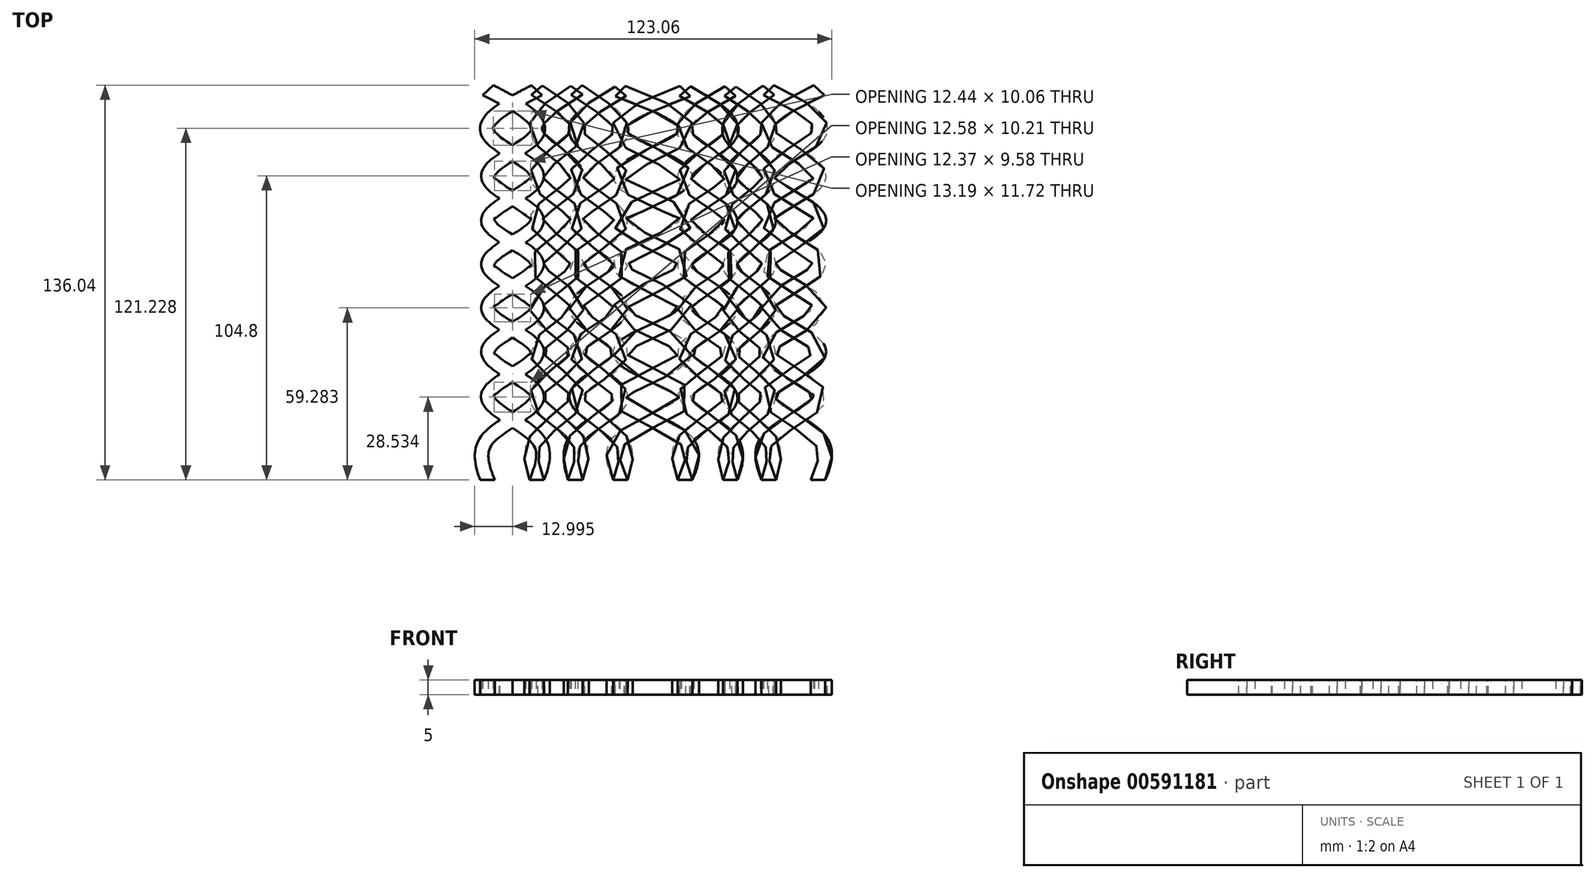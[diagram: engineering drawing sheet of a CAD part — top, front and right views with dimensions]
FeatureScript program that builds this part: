
annotation { "Feature Type Name" : "Feature", "Feature Type Description" : "" }
export const myFeature = defineFeature(function(context is Context, id is Id, definition is map)
    precondition{}
    {
        {
            var Q0;
            Q0=qCreatedBy(makeId("Front.planeOp"),FACE);
            var sketch = newSketch(context, id + "F0", { "sketchPlane" : qUnion([Q0])});
            skLineSegment(sketch, "E0.MirrorCS", {"start": v(59.45, 0) * mm, "end": v(54.45, 0) * mm});
            skLineSegment(sketch, "E1.MirrorCS", {"start": v(59.45, -5) * mm, "end": v(54.45, -5) * mm});
            skLineSegment(sketch, "E2.MirrorCS", {"start": v(59.45, 0) * mm, "end": v(59.45, -5) * mm});
            skLineSegment(sketch, "E3.MirrorCS", {"start": v(54.45, 0) * mm, "end": v(54.45, -5) * mm});
            skLineSegment(sketch, "E4.bottom", {"start": v(42.45, 0) * mm, "end": v(37.45, 0) * mm});
            skLineSegment(sketch, "E4.top", {"start": v(42.45, -5) * mm, "end": v(37.45, -5) * mm});
            skLineSegment(sketch, "E4.left", {"start": v(42.45, 0) * mm, "end": v(42.45, -5) * mm});
            skLineSegment(sketch, "E4.right", {"start": v(37.45, 0) * mm, "end": v(37.45, -5) * mm});
            skLineSegment(sketch, "E5.bottom", {"start": v(29.21, 0) * mm, "end": v(24.21, 0) * mm});
            skLineSegment(sketch, "E5.top", {"start": v(29.21, -5) * mm, "end": v(24.21, -5) * mm});
            skLineSegment(sketch, "E5.left", {"start": v(29.21, 0) * mm, "end": v(29.21, -5) * mm});
            skLineSegment(sketch, "E5.right", {"start": v(24.21, 0) * mm, "end": v(24.21, -5) * mm});
            skLineSegment(sketch, "E6", {"start": v(74.83, 0) * mm, "end": v(0, 0) * mm, "construction": true});
            skLineSegment(sketch, "E7.MirrorCS", {"start": v(-29.21, -5) * mm, "end": v(-24.21, -5) * mm});
            skLineSegment(sketch, "E8.MirrorCS", {"start": v(-29.21, 0) * mm, "end": v(-24.21, 0) * mm});
            skLineSegment(sketch, "E9.MirrorCS", {"start": v(-59.45, -5) * mm, "end": v(-54.45, -5) * mm});
            skLineSegment(sketch, "E10.MirrorCS", {"start": v(-42.45, -5) * mm, "end": v(-37.45, -5) * mm});
            skLineSegment(sketch, "E11.MirrorCS", {"start": v(-42.45, 0) * mm, "end": v(-37.45, 0) * mm});
            skLineSegment(sketch, "E12.MirrorCS", {"start": v(-59.45, 0) * mm, "end": v(-54.45, 0) * mm});
            skLineSegment(sketch, "E13.MirrorCS", {"start": v(-54.45, 0) * mm, "end": v(-54.45, -5) * mm});
            skLineSegment(sketch, "E14.MirrorCS", {"start": v(-59.45, 0) * mm, "end": v(-59.45, -5) * mm});
            skLineSegment(sketch, "E15.MirrorCS", {"start": v(-74.83, 0) * mm, "end": v(0, 0) * mm, "construction": true});
            skLineSegment(sketch, "E16.MirrorCS", {"start": v(-29.21, 0) * mm, "end": v(-29.21, -5) * mm});
            skLineSegment(sketch, "E17.MirrorCS", {"start": v(-37.45, 0) * mm, "end": v(-37.45, -5) * mm});
            skLineSegment(sketch, "E18.MirrorCS", {"start": v(-42.45, 0) * mm, "end": v(-42.45, -5) * mm});
            skLineSegment(sketch, "E19.MirrorCS", {"start": v(-24.21, 0) * mm, "end": v(-24.21, -5) * mm});
            skLineSegment(sketch, "E20.bottom", {"start": v(13.62, -5) * mm, "end": v(8.62, -5) * mm});
            skLineSegment(sketch, "E20.top", {"start": v(13.62, 0) * mm, "end": v(8.62, 0) * mm});
            skLineSegment(sketch, "E20.left", {"start": v(13.62, -5) * mm, "end": v(13.62, 0) * mm});
            skLineSegment(sketch, "E20.right", {"start": v(8.62, -5) * mm, "end": v(8.62, 0) * mm});
            skLineSegment(sketch, "E21.MirrorCS", {"start": v(-13.62, 0) * mm, "end": v(-8.62, 0) * mm});
            skLineSegment(sketch, "E22.MirrorCS", {"start": v(-13.62, -5) * mm, "end": v(-13.62, 0) * mm});
            skLineSegment(sketch, "E23.MirrorCS", {"start": v(-13.62, -5) * mm, "end": v(-8.62, -5) * mm});
            skLineSegment(sketch, "E24.MirrorCS", {"start": v(-8.62, -5) * mm, "end": v(-8.62, 0) * mm});
            skSolve(sketch);
        }
        {
            var Q0;
            Q0=qCreatedBy(makeId("Top.planeOp"),FACE);
            var sketch = newSketch(context, id + "F1", { "sketchPlane" : qUnion([Q0])});
            skPoint(sketch, "E25", {"position": v(26.71, 13.97) * mm});
            skPoint(sketch, "E26", {"position": v(39.95, 14.33) * mm});
            skPoint(sketch, "E27", {"position": v(57.32, 14.33) * mm});
            skPoint(sketch, "E28", {"position": v(-26.19, 14.33) * mm});
            skPoint(sketch, "E29", {"position": v(-39.95, 14.33) * mm});
            skPoint(sketch, "E30", {"position": v(-56.68, 14.33) * mm});
            skPoint(sketch, "E31", {"position": v(11.12, 13.97) * mm});
            skPoint(sketch, "E32", {"position": v(-11.12, 13.97) * mm});
            skPoint(sketch, "E33.0.1.0", {"position": v(11.12, 28.97) * mm});
            skPoint(sketch, "E33.0.1.1", {"position": v(-11.12, 28.97) * mm});
            skPoint(sketch, "E33.0.1.2", {"position": v(39.95, 29.33) * mm});
            skPoint(sketch, "E33.0.1.3", {"position": v(-56.68, 29.33) * mm});
            skPoint(sketch, "E33.0.1.4", {"position": v(57.32, 29.33) * mm});
            skPoint(sketch, "E33.0.1.5", {"position": v(-26.19, 29.33) * mm});
            skPoint(sketch, "E33.0.1.6", {"position": v(-39.95, 29.33) * mm});
            skPoint(sketch, "E33.0.1.7", {"position": v(26.71, 28.97) * mm});
            skPoint(sketch, "E33.0.2.0", {"position": v(11.12, 43.97) * mm});
            skPoint(sketch, "E33.0.2.1", {"position": v(-11.12, 43.97) * mm});
            skPoint(sketch, "E33.0.2.2", {"position": v(39.95, 44.33) * mm});
            skPoint(sketch, "E33.0.2.3", {"position": v(-56.68, 44.33) * mm});
            skPoint(sketch, "E33.0.2.4", {"position": v(57.32, 44.33) * mm});
            skPoint(sketch, "E33.0.2.5", {"position": v(-26.19, 44.33) * mm});
            skPoint(sketch, "E33.0.2.6", {"position": v(-39.95, 44.33) * mm});
            skPoint(sketch, "E33.0.2.7", {"position": v(26.71, 43.97) * mm});
            skPoint(sketch, "E33.0.3.0", {"position": v(11.12, 58.97) * mm});
            skPoint(sketch, "E33.0.3.1", {"position": v(-11.12, 58.97) * mm});
            skPoint(sketch, "E33.0.3.2", {"position": v(39.95, 59.33) * mm});
            skPoint(sketch, "E33.0.3.3", {"position": v(-56.68, 59.33) * mm});
            skPoint(sketch, "E33.0.3.4", {"position": v(57.32, 59.33) * mm});
            skPoint(sketch, "E33.0.3.5", {"position": v(-26.19, 59.33) * mm});
            skPoint(sketch, "E33.0.3.6", {"position": v(-39.95, 59.33) * mm});
            skPoint(sketch, "E33.0.3.7", {"position": v(26.71, 58.97) * mm});
            skPoint(sketch, "E33.0.4.0", {"position": v(11.12, 73.97) * mm});
            skPoint(sketch, "E33.0.4.1", {"position": v(-11.12, 73.97) * mm});
            skPoint(sketch, "E33.0.4.2", {"position": v(39.95, 74.33) * mm});
            skPoint(sketch, "E33.0.4.3", {"position": v(-56.68, 74.33) * mm});
            skPoint(sketch, "E33.0.4.4", {"position": v(57.32, 74.33) * mm});
            skPoint(sketch, "E33.0.4.5", {"position": v(-26.19, 74.33) * mm});
            skPoint(sketch, "E33.0.4.6", {"position": v(-39.95, 74.33) * mm});
            skPoint(sketch, "E33.0.4.7", {"position": v(26.71, 73.97) * mm});
            skPoint(sketch, "E33.0.5.0", {"position": v(11.12, 88.97) * mm});
            skPoint(sketch, "E33.0.5.1", {"position": v(-11.12, 88.97) * mm});
            skPoint(sketch, "E33.0.5.2", {"position": v(39.95, 89.33) * mm});
            skPoint(sketch, "E33.0.5.3", {"position": v(-56.68, 89.33) * mm});
            skPoint(sketch, "E33.0.5.4", {"position": v(57.32, 89.33) * mm});
            skPoint(sketch, "E33.0.5.5", {"position": v(-26.19, 89.33) * mm});
            skPoint(sketch, "E33.0.5.6", {"position": v(-39.95, 89.33) * mm});
            skPoint(sketch, "E33.0.5.7", {"position": v(26.71, 88.97) * mm});
            skPoint(sketch, "E33.0.6.0", {"position": v(11.12, 103.97) * mm});
            skPoint(sketch, "E33.0.6.1", {"position": v(-11.12, 103.97) * mm});
            skPoint(sketch, "E33.0.6.2", {"position": v(39.95, 104.33) * mm});
            skPoint(sketch, "E33.0.6.3", {"position": v(-56.68, 104.33) * mm});
            skPoint(sketch, "E33.0.6.4", {"position": v(57.32, 104.33) * mm});
            skPoint(sketch, "E33.0.6.5", {"position": v(-26.19, 104.33) * mm});
            skPoint(sketch, "E33.0.6.6", {"position": v(-39.95, 104.33) * mm});
            skPoint(sketch, "E33.0.6.7", {"position": v(26.71, 103.97) * mm});
            skPoint(sketch, "E33.0.7.0", {"position": v(11.12, 118.97) * mm});
            skPoint(sketch, "E33.0.7.1", {"position": v(-11.12, 118.97) * mm});
            skPoint(sketch, "E33.0.7.2", {"position": v(39.95, 119.33) * mm});
            skPoint(sketch, "E33.0.7.3", {"position": v(-56.68, 119.33) * mm});
            skPoint(sketch, "E33.0.7.4", {"position": v(57.32, 119.33) * mm});
            skPoint(sketch, "E33.0.7.5", {"position": v(-26.19, 119.33) * mm});
            skPoint(sketch, "E33.0.7.6", {"position": v(-39.95, 119.33) * mm});
            skPoint(sketch, "E33.0.7.7", {"position": v(26.71, 118.97) * mm});
            skPoint(sketch, "E33.0.8.0", {"position": v(11.12, 133.97) * mm});
            skPoint(sketch, "E33.0.8.1", {"position": v(-11.12, 133.97) * mm});
            skPoint(sketch, "E33.0.8.2", {"position": v(39.95, 134.33) * mm});
            skPoint(sketch, "E33.0.8.3", {"position": v(-56.68, 134.33) * mm});
            skPoint(sketch, "E33.0.8.4", {"position": v(57.32, 134.33) * mm});
            skPoint(sketch, "E33.0.8.5", {"position": v(-26.19, 134.33) * mm});
            skPoint(sketch, "E33.0.8.6", {"position": v(-39.95, 134.33) * mm});
            skPoint(sketch, "E33.0.8.7", {"position": v(26.71, 133.97) * mm});
            skLineSegment(sketch, "E33.direction1", {"start": v(-56.68, 14.33) * mm, "end": v(-31.68, 14.33) * mm, "construction": true});
            skLineSegment(sketch, "E33.direction2", {"start": v(-56.68, 14.33) * mm, "end": v(-56.68, 29.33) * mm, "construction": true});
            skFitSpline(sketch, "E34", {"points": [v(56.95, 0) * mm, v(57.32, 14.33) * mm, v(39.95, 29.33) * mm, v(57.32, 44.33) * mm, v(39.95, 59.33) * mm, v(57.32, 74.33) * mm, v(39.95, 89.33) * mm, v(57.32, 104.33) * mm, v(39.95, 119.33) * mm, v(57.32, 134.33) * mm], "startDerivative": vector(68.8, 168.07) * mm, "endDerivative": vector(275.05, 131.72) * mm});
            skFitSpline(sketch, "E35", {"points": [v(39.95, 0) * mm, v(39.95, 14.33) * mm, v(57.32, 29.33) * mm, v(39.95, 44.33) * mm, v(57.32, 59.33) * mm, v(39.95, 74.33) * mm, v(57.32, 89.33) * mm, v(39.95, 104.33) * mm, v(57.32, 119.33) * mm, v(39.95, 134.33) * mm], "startDerivative": vector(-65.2, 168.09) * mm, "endDerivative": vector(-275.05, 131.71) * mm});
            skFitSpline(sketch, "E36", {"points": [v(-56.95, 0) * mm, v(-56.68, 14.33) * mm, v(-39.95, 29.33) * mm, v(-56.68, 44.33) * mm, v(-39.95, 59.33) * mm, v(-56.68, 74.33) * mm, v(-39.95, 89.33) * mm, v(-56.68, 104.33) * mm, v(-39.95, 119.33) * mm, v(-56.68, 134.33) * mm], "startDerivative": vector(-59.74, 163.9) * mm, "endDerivative": vector(-254.01, 132) * mm});
            skFitSpline(sketch, "E37", {"points": [v(-39.95, 0) * mm, v(-39.95, 14.33) * mm, v(-56.68, 29.33) * mm, v(-39.95, 44.33) * mm, v(-56.68, 59.33) * mm, v(-39.95, 74.33) * mm, v(-56.68, 89.33) * mm, v(-39.95, 104.33) * mm, v(-56.68, 119.33) * mm, v(-39.95, 134.33) * mm], "startDerivative": vector(60.96, 163.9) * mm, "endDerivative": vector(254.01, 132) * mm});
            skFitSpline(sketch, "E38", {"points": [v(-26.71, 0) * mm, v(-26.19, 14.33) * mm, v(-39.95, 29.33) * mm, v(-26.19, 44.33) * mm, v(-39.95, 59.33) * mm, v(-26.19, 74.33) * mm, v(-39.95, 89.33) * mm, v(-26.19, 104.33) * mm, v(-39.95, 119.33) * mm, v(-26.19, 134.33) * mm], "startDerivative": vector(61.5, 155.56) * mm, "endDerivative": vector(211.71, 132.58) * mm});
            skFitSpline(sketch, "E39", {"points": [v(-39.95, 0) * mm, v(-39.95, 14.33) * mm, v(-26.19, 29.33) * mm, v(-39.95, 44.33) * mm, v(-26.19, 59.33) * mm, v(-39.95, 74.33) * mm, v(-26.19, 89.33) * mm, v(-39.95, 104.33) * mm, v(-26.19, 119.33) * mm, v(-39.95, 134.33) * mm], "startDerivative": vector(-52.05, 155.67) * mm, "endDerivative": vector(-211.7, 132.57) * mm});
            skFitSpline(sketch, "E40", {"points": [v(-26.71, 0) * mm, v(-26.19, 14.33) * mm, v(-11.12, 28.97) * mm, v(-26.19, 44.33) * mm, v(-11.12, 58.97) * mm, v(-26.19, 74.33) * mm, v(-11.12, 88.97) * mm, v(-26.19, 104.33) * mm, v(-11.12, 118.97) * mm, v(-26.19, 134.33) * mm], "startDerivative": vector(-41.22, 155.04) * mm, "endDerivative": vector(-203.36, 136.6) * mm});
            skFitSpline(sketch, "E41", {"points": [v(-11.12, 0) * mm, v(-11.12, 13.97) * mm, v(-26.19, 29.33) * mm, v(-11.12, 43.97) * mm, v(-26.19, 59.33) * mm, v(-11.12, 73.97) * mm, v(-26.19, 89.33) * mm, v(-11.12, 103.97) * mm, v(-26.19, 119.33) * mm, v(-11.12, 133.97) * mm], "startDerivative": vector(49.7, 150.67) * mm, "endDerivative": vector(203.88, 128.6) * mm});
            skFitSpline(sketch, "E42", {"points": [v(-11.12, 0) * mm, v(-11.12, 13.97) * mm, v(11.12, 28.97) * mm, v(-11.12, 43.97) * mm, v(11.12, 58.97) * mm, v(-11.12, 73.97) * mm, v(11.12, 88.97) * mm, v(-11.12, 103.97) * mm, v(11.12, 118.97) * mm, v(-11.12, 133.97) * mm], "startDerivative": vector(-78.52, 179.85) * mm, "endDerivative": vector(-347.84, 130.7) * mm});
            skFitSpline(sketch, "E43", {"points": [v(11.12, 0) * mm, v(11.12, 13.97) * mm, v(-11.12, 28.97) * mm, v(11.12, 43.97) * mm, v(-11.12, 58.97) * mm, v(11.12, 73.97) * mm, v(-11.12, 88.97) * mm, v(11.12, 103.97) * mm, v(-11.12, 118.97) * mm, v(11.12, 133.97) * mm], "startDerivative": vector(78.52, 179.85) * mm, "endDerivative": vector(347.84, 130.7) * mm});
            skFitSpline(sketch, "E44", {"points": [v(11.12, 0) * mm, v(11.12, 13.97) * mm, v(26.71, 28.97) * mm, v(11.12, 43.97) * mm, v(26.71, 58.97) * mm, v(11.12, 73.97) * mm, v(26.71, 88.97) * mm, v(11.12, 103.97) * mm, v(26.71, 118.97) * mm, v(11.12, 133.97) * mm], "startDerivative": vector(-58.34, 159.19) * mm, "endDerivative": vector(-243.19, 131.98) * mm});
            skFitSpline(sketch, "E45", {"points": [v(26.71, 0) * mm, v(26.71, 13.97) * mm, v(11.12, 28.97) * mm, v(26.71, 43.97) * mm, v(11.12, 58.97) * mm, v(26.71, 73.97) * mm, v(11.12, 88.97) * mm, v(26.71, 103.97) * mm, v(11.12, 118.97) * mm, v(26.71, 133.97) * mm], "startDerivative": vector(58.34, 159.19) * mm, "endDerivative": vector(243.19, 131.98) * mm});
            skFitSpline(sketch, "E46", {"points": [v(39.95, 0) * mm, v(39.95, 14.33) * mm, v(26.71, 28.97) * mm, v(39.95, 44.33) * mm, v(26.71, 58.97) * mm, v(39.95, 74.33) * mm, v(26.71, 88.97) * mm, v(39.95, 104.33) * mm, v(26.71, 118.97) * mm, v(39.95, 134.33) * mm], "startDerivative": vector(49.98, 154.65) * mm, "endDerivative": vector(200.69, 136.6) * mm});
            skFitSpline(sketch, "E47", {"points": [v(26.71, 0) * mm, v(26.71, 13.97) * mm, v(39.95, 29.33) * mm, v(26.71, 43.97) * mm, v(39.95, 59.33) * mm, v(26.71, 73.97) * mm, v(39.95, 89.33) * mm, v(26.71, 103.97) * mm, v(39.95, 119.33) * mm, v(26.71, 133.97) * mm], "startDerivative": vector(-49.12, 150.18) * mm, "endDerivative": vector(-201.23, 128.66) * mm});
            skSolve(sketch);
        }
        {
            var Q0;
            Q0=makeQuery(id+"F0.imprint","IMPRINT",FACE,{"disambiguationData":[TD([[makeQuery(id+"F0.imprint","IMPRINT",EDGE,{"derivedFrom":sQuery(id+"F0.wireOp",EDGE,"E9.MirrorCS")}),1.0]])]});
            var Q1;
            Q1=sQuery(id+"F1.wireOp",EDGE,"E36");
            sweep(context, id + "F2", {"profiles" : qUnion([Q0]), "path" : qUnion([Q1])});
        }
        {
            var Q0;
            Q0=makeQuery(id+"F0.imprint","IMPRINT",FACE,{"disambiguationData":[TD([[makeQuery(id+"F0.imprint","IMPRINT",EDGE,{"derivedFrom":sQuery(id+"F0.wireOp",EDGE,"E10.MirrorCS")}),1.0]])]});
            var Q1;
            Q1=sQuery(id+"F1.wireOp",EDGE,"E37");
            sweep(context, id + "F3", {"operationType" : NewBodyOperationType.ADD, "profiles" : qUnion([Q0]), "path" : qUnion([Q1])});
        }
        {
            var Q0;
            Q0=makeQuery(id+"F0.imprint","IMPRINT",FACE,{"disambiguationData":[TD([[makeQuery(id+"F0.imprint","IMPRINT",EDGE,{"derivedFrom":sQuery(id+"F0.wireOp",EDGE,"E7.MirrorCS")}),1.0]])]});
            var Q1;
            Q1=sQuery(id+"F1.wireOp",EDGE,"E40");
            sweep(context, id + "F4", {"profiles" : qUnion([Q0]), "path" : qUnion([Q1])});
        }
        {
            var Q0;
            Q0=makeQuery(id+"F0.imprint","IMPRINT",FACE,{"disambiguationData":[TD([[makeQuery(id+"F0.imprint","IMPRINT",EDGE,{"derivedFrom":sQuery(id+"F0.wireOp",EDGE,"E7.MirrorCS")}),1.0]])]});
            var Q1;
            Q1=sQuery(id+"F1.wireOp",EDGE,"E38");
            sweep(context, id + "F5", {"profiles" : qUnion([Q0]), "path" : qUnion([Q1])});
        }
        {
            var Q0;
            Q0=makeQuery(id+"F0.imprint","IMPRINT",FACE,{"disambiguationData":[TD([[makeQuery(id+"F0.imprint","IMPRINT",EDGE,{"derivedFrom":sQuery(id+"F0.wireOp",EDGE,"E10.MirrorCS")}),1.0]])]});
            var Q1;
            Q1=sQuery(id+"F1.wireOp",EDGE,"E39");
            sweep(context, id + "F6", {"profiles" : qUnion([Q0]), "path" : qUnion([Q1])});
        }
        {
            var Q0;
            Q0=makeQuery(id+"F0.imprint","IMPRINT",FACE,{"disambiguationData":[TD([[makeQuery(id+"F0.imprint","IMPRINT",EDGE,{"derivedFrom":sQuery(id+"F0.wireOp",EDGE,"E21.MirrorCS")}),-1.0]])]});
            var Q1;
            Q1=sQuery(id+"F1.wireOp",EDGE,"E42");
            sweep(context, id + "F7", {"profiles" : qUnion([Q0]), "path" : qUnion([Q1])});
        }
        {
            var Q0;
            Q0=makeQuery(id+"F0.imprint","IMPRINT",FACE,{"disambiguationData":[TD([[makeQuery(id+"F0.imprint","IMPRINT",EDGE,{"derivedFrom":sQuery(id+"F0.wireOp",EDGE,"E21.MirrorCS")}),-1.0]])]});
            var Q1;
            Q1=sQuery(id+"F1.wireOp",EDGE,"E41");
            sweep(context, id + "F8", {"profiles" : qUnion([Q0]), "path" : qUnion([Q1])});
        }
        {
            var Q0;
            Q0=makeQuery(id+"F0.imprint","IMPRINT",FACE,{"disambiguationData":[TD([[makeQuery(id+"F0.imprint","IMPRINT",EDGE,{"derivedFrom":sQuery(id+"F0.wireOp",EDGE,"E20.bottom")}),-1.0]])]});
            var Q1;
            Q1=sQuery(id+"F1.wireOp",EDGE,"E44");
            sweep(context, id + "F9", {"profiles" : qUnion([Q0]), "path" : qUnion([Q1])});
        }
        {
            var Q0;
            Q0=makeQuery(id+"F0.imprint","IMPRINT",FACE,{"disambiguationData":[TD([[makeQuery(id+"F0.imprint","IMPRINT",EDGE,{"derivedFrom":sQuery(id+"F0.wireOp",EDGE,"E20.bottom")}),-1.0]])]});
            var Q1;
            Q1=sQuery(id+"F1.wireOp",EDGE,"E43");
            sweep(context, id + "F10", {"profiles" : qUnion([Q0]), "path" : qUnion([Q1])});
        }
        {
            var Q0;
            Q0=makeQuery(id+"F0.imprint","IMPRINT",FACE,{"disambiguationData":[TD([[makeQuery(id+"F0.imprint","IMPRINT",EDGE,{"derivedFrom":sQuery(id+"F0.wireOp",EDGE,"E5.bottom")}),1.0]])]});
            var Q1;
            Q1=sQuery(id+"F1.wireOp",EDGE,"E45");
            sweep(context, id + "F11", {"profiles" : qUnion([Q0]), "path" : qUnion([Q1])});
        }
        {
            var Q0;
            Q0=makeQuery(id+"F0.imprint","IMPRINT",FACE,{"disambiguationData":[TD([[makeQuery(id+"F0.imprint","IMPRINT",EDGE,{"derivedFrom":sQuery(id+"F0.wireOp",EDGE,"E4.bottom")}),1.0]])]});
            var Q1;
            Q1=sQuery(id+"F1.wireOp",EDGE,"E35");
            sweep(context, id + "F12", {"profiles" : qUnion([Q0]), "path" : qUnion([Q1])});
        }
        {
            var Q0;
            Q0=makeQuery(id+"F0.imprint","IMPRINT",FACE,{"disambiguationData":[TD([[makeQuery(id+"F0.imprint","IMPRINT",EDGE,{"derivedFrom":sQuery(id+"F0.wireOp",EDGE,"E4.bottom")}),1.0]])]});
            var Q1;
            Q1=sQuery(id+"F1.wireOp",EDGE,"E46");
            sweep(context, id + "F13", {"profiles" : qUnion([Q0]), "path" : qUnion([Q1])});
        }
        {
            var Q0;
            Q0=makeQuery(id+"F0.imprint","IMPRINT",FACE,{"disambiguationData":[TD([[makeQuery(id+"F0.imprint","IMPRINT",EDGE,{"derivedFrom":sQuery(id+"F0.wireOp",EDGE,"E5.bottom")}),1.0]])]});
            var Q1;
            Q1=sQuery(id+"F1.wireOp",EDGE,"E47");
            sweep(context, id + "F14", {"profiles" : qUnion([Q0]), "path" : qUnion([Q1])});
        }
        {
            var Q0;
            Q0=makeQuery(id+"F0.imprint","IMPRINT",FACE,{"disambiguationData":[TD([[makeQuery(id+"F0.imprint","IMPRINT",EDGE,{"derivedFrom":sQuery(id+"F0.wireOp",EDGE,"E0.MirrorCS")}),1.0]])]});
            var Q1;
            Q1=sQuery(id+"F1.wireOp",EDGE,"E34");
            sweep(context, id + "F15", {"profiles" : qUnion([Q0]), "path" : qUnion([Q1])});
        }
        {
            var Q0;
            Q0=makeQuery(id+"F0.imprint","IMPRINT",FACE,{"disambiguationData":[TD([[makeQuery(id+"F0.imprint","IMPRINT",EDGE,{"derivedFrom":sQuery(id+"F0.wireOp",EDGE,"E20.bottom")}),-1.0]])]});
            var Q1;
            Q1=sQuery(id+"F1.wireOp",EDGE,"E43");
            sweep(context, id + "F16", {"profiles" : qUnion([Q0]), "path" : qUnion([Q1])});
        }
    });
